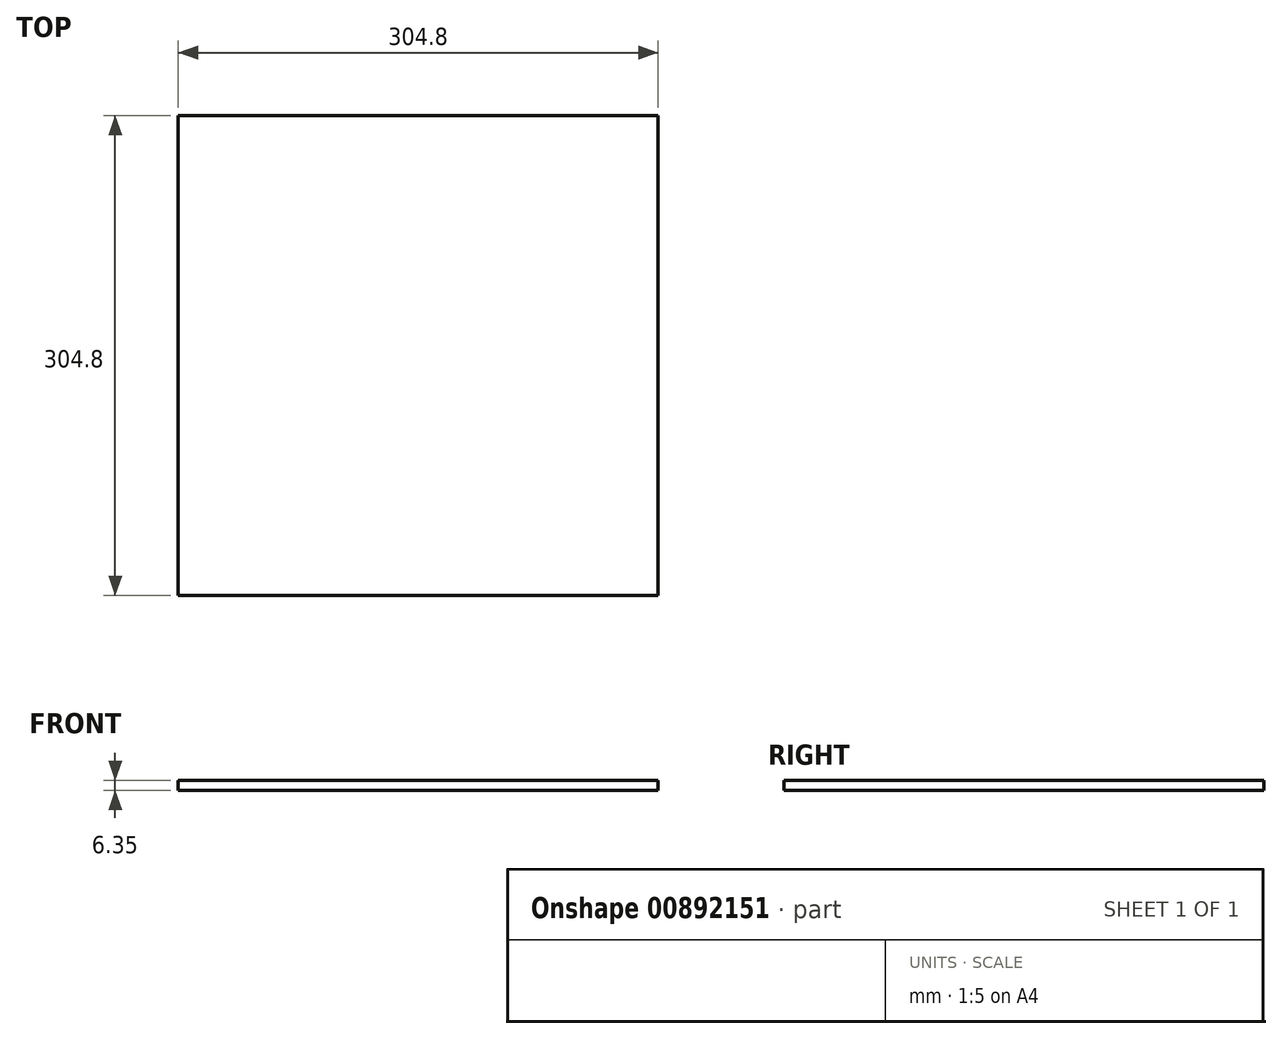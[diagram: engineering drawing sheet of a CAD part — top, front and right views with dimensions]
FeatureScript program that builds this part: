
annotation { "Feature Type Name" : "Feature", "Feature Type Description" : "" }
export const myFeature = defineFeature(function(context is Context, id is Id, definition is map)
    precondition{}
    {
        {
            var Q0;
            Q0=qCreatedBy(makeId("Top.planeOp"),FACE);
            var sketch = newSketch(context, id + "F0", { "sketchPlane" : qUnion([Q0])});
            skLineSegment(sketch, "E0.bottom", {"start": v(152.4, -152.4) * mm, "end": v(-152.4, -152.4) * mm});
            skLineSegment(sketch, "E0.top", {"start": v(152.4, 152.4) * mm, "end": v(-152.4, 152.4) * mm});
            skLineSegment(sketch, "E0.left", {"start": v(152.4, -152.4) * mm, "end": v(152.4, 152.4) * mm});
            skLineSegment(sketch, "E0.right", {"start": v(-152.4, -152.4) * mm, "end": v(-152.4, 152.4) * mm});
            skPoint(sketch, "E0.middle", {"position": v(0, 0) * mm});
            skSolve(sketch);
        }
        {
            var Q0;
            Q0 = qSketchRegion(id + "F0", true);
            extrude(context, id + "F1", {"entities" : qUnion([Q0]), "oppositeDirection" : true, "depth" : 6.35 * mm, "offsetDistance" : 25.4 * mm});
        }
    });
